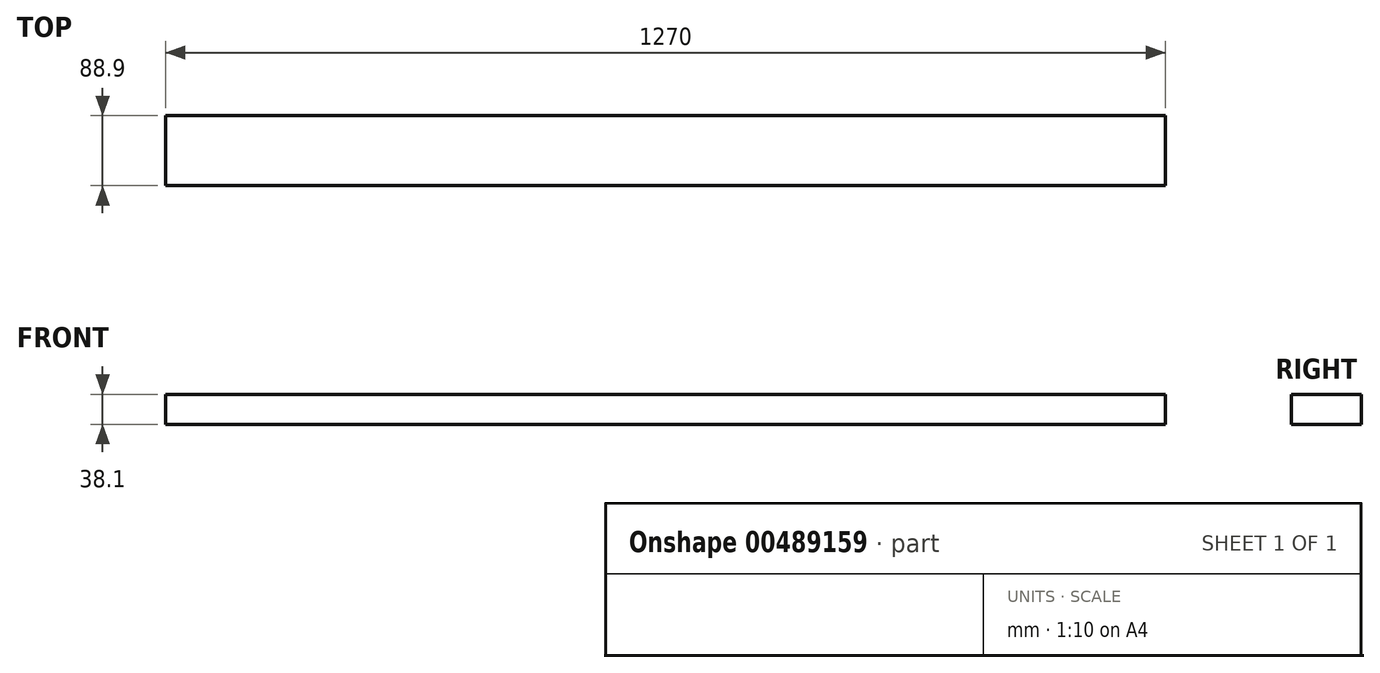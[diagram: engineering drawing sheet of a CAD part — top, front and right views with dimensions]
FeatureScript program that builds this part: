
annotation { "Feature Type Name" : "Feature", "Feature Type Description" : "" }
export const myFeature = defineFeature(function(context is Context, id is Id, definition is map)
    precondition{}
    {
        {
            var Q0;
            Q0=qCreatedBy(makeId("Top.planeOp"),FACE);
            var sketch = newSketch(context, id + "F0", { "sketchPlane" : qUnion([Q0])});
            skLineSegment(sketch, "E0.bottom", {"start": v(-629.13, 36.07) * mm, "end": v(640.87, 36.07) * mm});
            skLineSegment(sketch, "E0.top", {"start": v(-629.13, -52.83) * mm, "end": v(640.87, -52.83) * mm});
            skLineSegment(sketch, "E0.left", {"start": v(-629.13, 36.07) * mm, "end": v(-629.13, -52.83) * mm});
            skLineSegment(sketch, "E0.right", {"start": v(640.87, 36.07) * mm, "end": v(640.87, -52.83) * mm});
            skSolve(sketch);
        }
        {
            var Q0;
            Q0=makeQuery(id+"F0.imprint","IMPRINT",FACE,{"disambiguationData":[TD([[makeQuery(id+"F0.imprint","IMPRINT",EDGE,{"derivedFrom":sQuery(id+"F0.wireOp",EDGE,"E0.bottom")}),-1.0]])]});
            extrude(context, id + "F1", {"entities" : qUnion([Q0]), "depth" : 38.1 * mm, "offsetDistance" : 25.4 * mm, "symmetric" : true});
        }
    });
